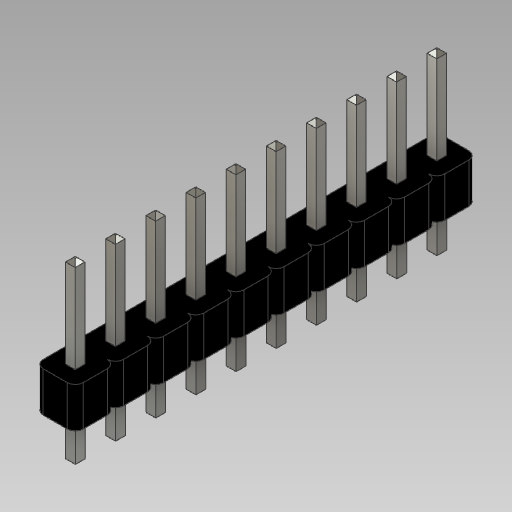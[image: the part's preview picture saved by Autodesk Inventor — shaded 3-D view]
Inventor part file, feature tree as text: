
AUTODESK INVENTOR PART (.ipt)
format: ipt  version: 2020 (Build 240168000, 168)  size: 676,864 bytes
history: native  units: in
note: dims shown in document units (in); Inventor stores cm internally (conversion verified against a paired STEP export)
features: other x6, extrude x4, sketch x3, chamfer x2
ambient origin geometry x8: Origin, YZ Plane, XZ Plane, XY Plane, X Axis, Y Axis, Z Axis, Center Point
bodies: Solid1 (feature_tree)
feature tree (15):
  extrude  "Extrusion1"  Depth=0.02in
  extrude  "Extrusion2"  Depth=0.1in TaperAngle=0.0deg
  chamfer  "Chamfer2"  Distance=0.1in
  extrude  "Extrusion3"  Depth=0.23in TaperAngle=0.0deg
  chamfer  "Chamfer4"  Distance=0.01in Angle=45.0deg
  other  "Work Point1"
  other  "Work Point2"
  other  "Work Axis1"
  other  "Work Axis2"
  extrude  "Extrusion4"  Depth=0.1in
  other  "Work Axis3"
  sketch  "Sketch1"  dims[d0=0.1in d1=0.02in]
  sketch  "Sketch2"  dims[d2=6.2992in d4=0.1in d5=0.3937in d7=1.0in d9=0.1in d10=0.0in]
  sketch  "Sketch6"  dims[d11=0.024in d12=6.2992in d14=0.1in d15=0.3937in d17=1.0in d19=0.23in d20=0.0in d26=0.01in d27=0.125in d28=45.0deg d29=6.2992in d31=0.1in d32=0.3937in d34=1.0in d36=0.114in d37=0.0in d41=0.01in d42=0.125in d43=45.0deg d46=0.0in d47=0.0in]
  other  "Work Point3"
